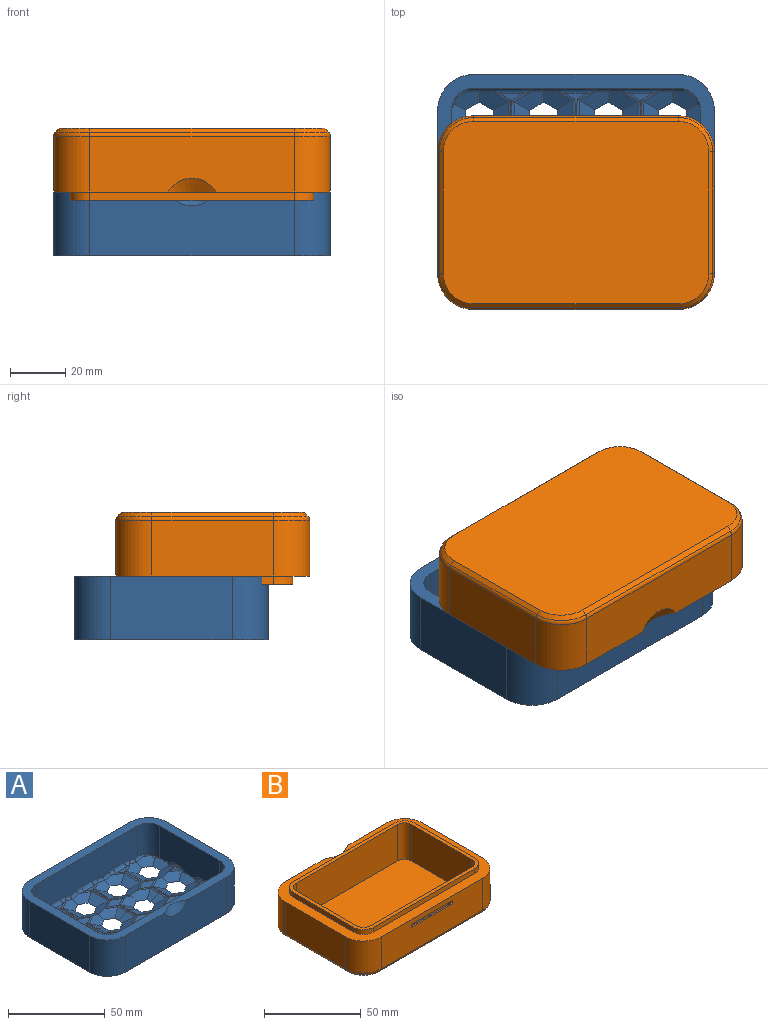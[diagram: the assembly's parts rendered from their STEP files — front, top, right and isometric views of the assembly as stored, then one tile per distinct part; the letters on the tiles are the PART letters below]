
ASSEMBLY  parts=2 mates=2
PART A: 247 faces, bbox 103.5x73.5x29 mm
  f0: plane 103.46x73.46mm, normal (0,0,1), area 1477.7mm2, adj f2,f4,f11,f16,f66,f67,f68,f74
  f1: plane 30x3mm, normal (0,-1,0), area 90mm2, adj f240,f241,f243,f244
  f2: plane 74x23mm, normal (0,1,0), area 1642mm2, adj f0,f3,f67,f127,f240,f241,f244,f245
  f3: plane 100x70mm, normal (0,0,-1), area 5815.7mm2, adj f2,f4,f7,f8,f9,f10,f21,f22
  f4: plane 44x23mm, normal (-1,0,0), area 1012mm2, adj f0,f3,f67,f185
  f5: plane 56x10.72mm, normal (0,0,1), area 99.6mm2, adj f12,f13,f39,f41,f43,f44,f47,f48
  f6: plane 25.94x10.76mm, normal (0,0,1), area 74.7mm2, adj f14,f17,f46,f77,f78,f106,f132,f135
  f7: plane 6.19x5.6mm, normal (-0.45,0,0.89), area 28.4mm2, adj f3,f14,f27,f129
  f8: plane 6.02x5.63mm, normal (0.45,0,0.89), area 27.7mm2, adj f3,f13,f28,f130
  f9: plane 12.21x5.58mm, normal (-0.45,0,0.89), area 56.1mm2, adj f3,f12,f32,f150
  f10: plane 12.1x7.11mm, normal (0.45,0,0.89), area 45.6mm2, adj f3,f11,f34,f65,f152,f183
  f11: plane 44x20.5mm, normal (1,0,0), area 852.2mm2, adj f0,f10,f35,f37,f59,f60,f62,f64
  f12: cylinder r=2mm len=13.25mm, axis (0,-1,0), area 11.8mm2, adj f5,f9,f39,f157
  f13: cylinder r=2mm len=6.55mm, axis (-0.01,1,0), area 5.8mm2, adj f5,f8,f43,f131
  f14: cylinder r=2mm len=6.72mm, axis (0.01,-1,0), area 6mm2, adj f6,f7,f46,f132
  f15: plane 14.57x7.49mm, normal (0,0,1), area 12.7mm2, adj f18,f19,f54,f79,f114
  f16: plane 74.05x19.52mm, normal (0,-1,0), area 1363.5mm2, adj f0,f19,f45,f49,f51,f53,f55,f56
  f17: cylinder r=2mm len=7.14mm, axis (-0.85,-0.53,0), area 6.4mm2, adj f6,f18,f26,f46,f78
  f18: cylinder r=2mm len=13.26mm, axis (0.03,-1,0), area 11.8mm2, adj f15,f17,f25,f54,f79
  f19: cylinder r=2mm len=7.49mm, axis (-1,0,0), area 23.5mm2, adj f15,f16,f56,f116
  f20: plane 1.98x1.71mm, normal (0,0,1), area 1.7mm2, adj f61,f62,f63
  f21: plane 10.68x6.52mm, normal (-0.21,-0.39,0.89), area 48.9mm2, adj f3,f22,f25,f54,f57,f58
  f22: plane 10.58x6.81mm, normal (0.24,-0.38,0.89), area 49.5mm2, adj f3,f21,f29,f52,f57
  f23: plane 10.58x6.67mm, normal (-0.22,-0.39,0.89), area 49.2mm2, adj f3,f24,f31,f48,f49
  f24: plane 8.46x6.65mm, normal (0.22,-0.39,0.89), area 46.3mm2, adj f3,f23,f35,f37,f40,f45,f49
  f25: plane 12.21x5.87mm, normal (-0.45,-0.01,0.89), area 56.1mm2, adj f3,f18,f21,f26
  f26: plane 10.58x7mm, normal (-0.24,0.38,0.89), area 50.2mm2, adj f3,f17,f25,f27,f30
  f27: plane 10.61x6.79mm, normal (-0.22,-0.39,0.89), area 49.1mm2, adj f3,f7,f26,f28,f30,f46
  f28: plane 10.58x6.87mm, normal (0.23,-0.39,0.89), area 49.9mm2, adj f3,f8,f27,f30,f43
  f29: plane 12.21x5.87mm, normal (0.45,0.01,0.89), area 56.1mm2, adj f3,f22,f30,f50
  f30: plane 10.69x6.67mm, normal (0.21,0.39,0.89), area 48.9mm2, adj f3,f26,f27,f28,f29,f47
  f31: plane 12.21x5.59mm, normal (-0.45,0,0.89), area 56.1mm2, adj f3,f23,f33,f44
  f32: plane 10.58x6.73mm, normal (-0.22,-0.39,0.89), area 49.6mm2, adj f3,f9,f33,f34,f39
  f33: plane 10.58x6.72mm, normal (-0.22,0.39,0.89), area 49.5mm2, adj f3,f31,f32,f34,f36,f41
  f34: plane 8.45x6.73mm, normal (0.22,-0.39,0.89), area 46.6mm2, adj f3,f10,f32,f33,f36,f63,f65
  f35: plane 12.09x7.11mm, normal (0.45,0,0.89), area 45.6mm2, adj f3,f11,f24,f36,f37,f59
  f36: plane 8.44x6.74mm, normal (0.22,0.39,0.89), area 46.6mm2, adj f3,f33,f34,f35,f59,f61
  f37: cylinder r=2mm len=5.56mm, axis (0,-0.92,-0.4), area 3.4mm2, adj f11,f24,f35,f38,f66
  f38: bspline ~2.22x1.86mm, area 0mm2, adj f37,f40,f66
  f39: cylinder r=2mm len=6.97mm, axis (0.87,-0.5,0), area 6mm2, adj f5,f12,f32,f41
  f40: cylinder r=2mm len=4.19mm, axis (0.87,0.5,0), area 1.8mm2, adj f24,f38,f42,f66
  f41: cylinder r=2mm len=6.96mm, axis (-0.87,-0.5,0), area 6mm2, adj f5,f33,f39,f44
  f42: bspline ~4.88x2.29mm, area 1.4mm2, adj f40,f45,f66
  f43: cylinder r=2mm len=7.04mm, axis (0.86,0.51,0), area 6.1mm2, adj f5,f13,f28,f47
  f44: cylinder r=2mm len=13.25mm, axis (0,-1,0), area 11.8mm2, adj f5,f31,f41,f48
  f45: cylinder r=2mm len=5.08mm, axis (-0.97,0,0.24), area 9.2mm2, adj f16,f24,f42,f49,f66
  f46: cylinder r=2mm len=6.89mm, axis (0.87,-0.49,0), area 5.9mm2, adj f6,f14,f17,f27
  f47: cylinder r=2mm len=6.76mm, axis (-0.88,0.47,0), area 5.7mm2, adj f5,f30,f43,f50
  f48: cylinder r=2mm len=6.86mm, axis (0.87,-0.5,0), area 5.2mm2, adj f5,f23,f44,f51
  f49: cylinder r=2mm len=5.05mm, axis (-0.97,0,-0.24), area 10.7mm2, adj f16,f23,f24,f45,f51
  f50: cylinder r=2mm len=13.27mm, axis (-0.03,1,0), area 11.8mm2, adj f5,f29,f47,f52
  f51: bspline ~5.67x2.36mm, area 9.1mm2, adj f16,f48,f49,f53
  f52: cylinder r=2mm len=6.98mm, axis (0.85,0.53,0), area 5.5mm2, adj f5,f22,f50,f55
  f53: cylinder r=2mm len=7.98mm, axis (-1,0,0), area 25.1mm2, adj f5,f16,f51,f55
  f54: cylinder r=2mm len=6.7mm, axis (0.88,-0.47,0), area 4.8mm2, adj f15,f18,f21,f56
  f55: bspline ~3.39x2.21mm, area 8.6mm2, adj f16,f52,f53,f57
  f56: bspline ~3.79x2.21mm, area 9.7mm2, adj f16,f19,f54,f58
  f57: cylinder r=2mm len=4.86mm, axis (-0.97,0,0.26), area 10.3mm2, adj f16,f21,f22,f55,f58
  f58: cylinder r=2mm len=5.28mm, axis (-0.97,0,-0.23), area 11.1mm2, adj f16,f21,f56,f57
  f59: cylinder r=2mm len=5.58mm, axis (0,-0.92,0.4), area 10.7mm2, adj f11,f35,f36,f60
  f60: bspline ~2.21x2.07mm, area 4.7mm2, adj f11,f59,f61,f62
  f61: cylinder r=2mm len=4.39mm, axis (-0.87,0.5,0), area 3mm2, adj f20,f36,f60,f63
  f62: cylinder r=2mm len=2mm, axis (0,-1,0), area 6.2mm2, adj f11,f20,f60,f64
  f63: cylinder r=2mm len=4.39mm, axis (0.87,0.5,0), area 3mm2, adj f20,f34,f61,f64
  f64: bspline ~2.69x2.31mm, area 4.7mm2, adj f11,f62,f63,f65
  f65: cylinder r=2mm len=5.57mm, axis (0,-0.92,-0.4), area 10.6mm2, adj f10,f11,f34,f64
  f66: cylinder r=8mm len=20.18mm, axis (0,0,-1), area 249.6mm2, adj f0,f11,f16,f37,f38,f40,f42,f45
  f67: cylinder r=13mm len=23mm, axis (0,0,1), area 469.7mm2, adj f0,f2,f3,f4
  f68: plane 44x23mm, normal (1,0,0), area 1012mm2, adj f0,f3,f127,f239
  f69: plane 56x10.72mm, normal (0,0,1), area 99.6mm2, adj f75,f76,f99,f101,f103,f104,f107,f108
  f70: plane 6.19x5.6mm, normal (0.45,0,0.89), area 28.4mm2, adj f3,f77,f87,f186
  f71: plane 6.02x5.63mm, normal (-0.45,0,0.89), area 27.7mm2, adj f3,f76,f88,f187
  f72: plane 12.21x5.58mm, normal (0.45,0,0.89), area 56.1mm2, adj f3,f75,f92,f204
  f73: plane 12.1x7.11mm, normal (-0.45,0,0.89), area 45.6mm2, adj f3,f74,f94,f125,f206,f237
  f74: plane 44x20.5mm, normal (-1,0,0), area 852.2mm2, adj f0,f73,f95,f97,f119,f120,f122,f124
  f75: cylinder r=2mm len=13.25mm, axis (0,-1,0), area 11.8mm2, adj f69,f72,f99,f211
  f76: cylinder r=2mm len=6.55mm, axis (0.01,1,0), area 5.8mm2, adj f69,f71,f103,f188
  f77: cylinder r=2mm len=6.72mm, axis (-0.01,-1,0), area 6mm2, adj f6,f70,f106,f189
  f78: cylinder r=2mm len=7.14mm, axis (0.85,-0.53,0), area 6.4mm2, adj f6,f17,f79,f86,f106
  f79: cylinder r=2mm len=13.26mm, axis (-0.03,-1,0), area 11.8mm2, adj f15,f18,f78,f85,f114
  f80: plane 1.98x1.71mm, normal (0,0,1), area 1.7mm2, adj f121,f122,f123
  f81: plane 10.68x6.52mm, normal (0.21,-0.39,0.89), area 48.9mm2, adj f3,f82,f85,f114,f117,f118
  f82: plane 10.58x6.81mm, normal (-0.24,-0.38,0.89), area 49.5mm2, adj f3,f81,f89,f112,f117
  f83: plane 10.58x6.67mm, normal (0.22,-0.39,0.89), area 49.2mm2, adj f3,f84,f91,f108,f109
  f84: plane 8.46x6.65mm, normal (-0.22,-0.39,0.89), area 46.3mm2, adj f3,f83,f95,f97,f100,f105,f109
  f85: plane 12.21x5.87mm, normal (0.45,-0.01,0.89), area 56.1mm2, adj f3,f79,f81,f86
  f86: plane 10.58x7mm, normal (0.24,0.38,0.89), area 50.2mm2, adj f3,f78,f85,f87,f90
  f87: plane 10.61x6.79mm, normal (0.22,-0.39,0.89), area 49.1mm2, adj f3,f70,f86,f88,f90,f106
  f88: plane 10.58x6.87mm, normal (-0.23,-0.39,0.89), area 49.9mm2, adj f3,f71,f87,f90,f103
  f89: plane 12.21x5.87mm, normal (-0.45,0.01,0.89), area 56.1mm2, adj f3,f82,f90,f110
  f90: plane 10.69x6.67mm, normal (-0.21,0.39,0.89), area 48.9mm2, adj f3,f86,f87,f88,f89,f107
  f91: plane 12.21x5.59mm, normal (0.45,0,0.89), area 56.1mm2, adj f3,f83,f93,f104
  f92: plane 10.58x6.73mm, normal (0.22,-0.39,0.89), area 49.6mm2, adj f3,f72,f93,f94,f99
  f93: plane 10.58x6.72mm, normal (0.22,0.39,0.89), area 49.5mm2, adj f3,f91,f92,f94,f96,f101
  f94: plane 8.45x6.73mm, normal (-0.22,-0.39,0.89), area 46.6mm2, adj f3,f73,f92,f93,f96,f123,f125
  f95: plane 12.09x7.11mm, normal (-0.45,0,0.89), area 45.6mm2, adj f3,f74,f84,f96,f97,f119
  f96: plane 8.44x6.74mm, normal (-0.22,0.39,0.89), area 46.6mm2, adj f3,f93,f94,f95,f119,f121
  f97: cylinder r=2mm len=5.56mm, axis (0,-0.92,-0.4), area 3.4mm2, adj f74,f84,f95,f98,f126
  f98: bspline ~2.22x1.86mm, area 0mm2, adj f97,f100,f126
  f99: cylinder r=2mm len=6.97mm, axis (-0.87,-0.5,0), area 6mm2, adj f69,f75,f92,f101
  f100: cylinder r=2mm len=4.19mm, axis (-0.87,0.5,0), area 1.8mm2, adj f84,f98,f102,f126
  f101: cylinder r=2mm len=6.96mm, axis (0.87,-0.5,0), area 6mm2, adj f69,f93,f99,f104
  f102: bspline ~4.56x2.29mm, area 1.4mm2, adj f100,f105,f126
  f103: cylinder r=2mm len=7.04mm, axis (-0.86,0.51,0), area 6.1mm2, adj f69,f76,f88,f107
  f104: cylinder r=2mm len=13.25mm, axis (0,-1,0), area 11.8mm2, adj f69,f91,f101,f108
  f105: cylinder r=2mm len=5.08mm, axis (0.97,0,0.24), area 9.2mm2, adj f16,f84,f102,f109,f126
  f106: cylinder r=2mm len=6.89mm, axis (-0.87,-0.49,0), area 5.9mm2, adj f6,f77,f78,f87
  f107: cylinder r=2mm len=6.76mm, axis (0.88,0.47,0), area 5.7mm2, adj f69,f90,f103,f110
  f108: cylinder r=2mm len=6.86mm, axis (-0.87,-0.5,0), area 5.2mm2, adj f69,f83,f104,f111
  f109: cylinder r=2mm len=5.05mm, axis (0.97,0,-0.24), area 10.7mm2, adj f16,f83,f84,f105,f111
  f110: cylinder r=2mm len=13.27mm, axis (0.03,1,0), area 11.8mm2, adj f69,f89,f107,f112
  f111: bspline ~5.67x2.36mm, area 9.1mm2, adj f16,f108,f109,f113
  f112: cylinder r=2mm len=6.98mm, axis (-0.85,0.53,0), area 5.5mm2, adj f69,f82,f110,f115
  f113: cylinder r=2mm len=7.98mm, axis (1,0,0), area 25.1mm2, adj f16,f69,f111,f115
  f114: cylinder r=2mm len=6.7mm, axis (-0.88,-0.47,0), area 4.8mm2, adj f15,f79,f81,f116
  f115: bspline ~3.39x2.21mm, area 8.6mm2, adj f16,f112,f113,f117
  f116: bspline ~3.79x2.21mm, area 9.7mm2, adj f16,f19,f114,f118
  f117: cylinder r=2mm len=4.86mm, axis (0.97,0,0.26), area 10.3mm2, adj f16,f81,f82,f115,f118
  f118: cylinder r=2mm len=5.28mm, axis (0.97,0,-0.23), area 11.1mm2, adj f16,f81,f116,f117
  f119: cylinder r=2mm len=5.58mm, axis (0,-0.92,0.4), area 10.7mm2, adj f74,f95,f96,f120
  f120: bspline ~2.21x2.07mm, area 4.7mm2, adj f74,f119,f121,f122
  f121: cylinder r=2mm len=4.39mm, axis (0.87,0.5,0), area 3mm2, adj f80,f96,f120,f123
  f122: cylinder r=2mm len=2mm, axis (0,-1,0), area 6.2mm2, adj f74,f80,f120,f124
  f123: cylinder r=2mm len=4.39mm, axis (-0.87,0.5,0), area 3mm2, adj f80,f94,f121,f124
  f124: bspline ~2.69x2.31mm, area 4.7mm2, adj f74,f122,f123,f125
  f125: cylinder r=2mm len=5.57mm, axis (0,-0.92,-0.4), area 10.6mm2, adj f73,f74,f94,f124
  f126: cylinder r=8mm len=20.18mm, axis (0,0,-1), area 249.6mm2, adj f0,f16,f74,f97,f98,f100,f102,f105
  f127: cylinder r=13mm len=23mm, axis (0,0,1), area 469.7mm2, adj f0,f2,f3,f68
  f128: plane 74x23mm, normal (0,-1,0), area 1640.6mm2, adj f0,f3,f185,f239,f246
  f129: plane 6.19x5.6mm, normal (-0.45,0,0.89), area 28.4mm2, adj f3,f7,f132,f145
  f130: plane 6.02x5.63mm, normal (0.45,0,0.89), area 27.7mm2, adj f3,f8,f131,f146
  f131: cylinder r=2mm len=6.55mm, axis (-0.01,-1,0), area 5.8mm2, adj f5,f13,f130,f161
  f132: cylinder r=2mm len=6.72mm, axis (0.01,1,0), area 6mm2, adj f6,f14,f129,f164
  f133: plane 14.57x7.49mm, normal (0,0,1), area 12.7mm2, adj f136,f137,f172,f191,f226
  f134: plane 74.05x19.52mm, normal (0,1,0), area 1363.5mm2, adj f0,f137,f163,f167,f169,f171,f173,f174
  f135: cylinder r=2mm len=7.14mm, axis (-0.85,0.53,0), area 6.4mm2, adj f6,f136,f144,f164,f190
  f136: cylinder r=2mm len=13.26mm, axis (0.03,1,0), area 11.8mm2, adj f133,f135,f143,f172,f191
  f137: cylinder r=2mm len=7.49mm, axis (-1,0,0), area 23.5mm2, adj f133,f134,f174,f228
  f138: plane 1.98x1.71mm, normal (0,0,1), area 1.7mm2, adj f179,f180,f181
  f139: plane 10.68x6.52mm, normal (-0.21,0.39,0.89), area 48.9mm2, adj f3,f140,f143,f172,f175,f176
  f140: plane 10.58x6.81mm, normal (0.24,0.38,0.89), area 49.5mm2, adj f3,f139,f147,f170,f175
  f141: plane 10.58x6.67mm, normal (-0.22,0.39,0.89), area 49.2mm2, adj f3,f142,f149,f166,f167
  f142: plane 8.46x6.65mm, normal (0.22,0.39,0.89), area 46.3mm2, adj f3,f141,f153,f155,f158,f163,f167
  f143: plane 12.21x5.87mm, normal (-0.45,0.01,0.89), area 56.1mm2, adj f3,f136,f139,f144
  f144: plane 10.58x7mm, normal (-0.24,-0.38,0.89), area 50.2mm2, adj f3,f135,f143,f145,f148
  f145: plane 10.61x6.79mm, normal (-0.22,0.39,0.89), area 49.1mm2, adj f3,f129,f144,f146,f148,f164
  f146: plane 10.58x6.87mm, normal (0.23,0.39,0.89), area 49.9mm2, adj f3,f130,f145,f148,f161
  f147: plane 12.21x5.87mm, normal (0.45,-0.01,0.89), area 56.1mm2, adj f3,f140,f148,f168
  f148: plane 10.69x6.67mm, normal (0.21,-0.39,0.89), area 48.9mm2, adj f3,f144,f145,f146,f147,f165
  f149: plane 12.21x5.59mm, normal (-0.45,0,0.89), area 56.1mm2, adj f3,f141,f151,f162
  f150: plane 10.58x6.73mm, normal (-0.22,0.39,0.89), area 49.6mm2, adj f3,f9,f151,f152,f157
  f151: plane 10.58x6.72mm, normal (-0.22,-0.39,0.89), area 49.5mm2, adj f3,f149,f150,f152,f154,f159
  f152: plane 8.45x6.73mm, normal (0.22,0.39,0.89), area 46.6mm2, adj f3,f10,f150,f151,f154,f181,f183
  f153: plane 12.09x7.11mm, normal (0.45,0,0.89), area 45.6mm2, adj f3,f11,f142,f154,f155,f177
  f154: plane 8.44x6.74mm, normal (0.22,-0.39,0.89), area 46.6mm2, adj f3,f151,f152,f153,f177,f179
  f155: cylinder r=2mm len=5.56mm, axis (0,0.92,-0.4), area 3.4mm2, adj f11,f142,f153,f156,f184
  f156: bspline ~2.22x1.86mm, area 0mm2, adj f155,f158,f184
  f157: cylinder r=2mm len=6.97mm, axis (0.87,0.5,0), area 6mm2, adj f5,f12,f150,f159
  f158: cylinder r=2mm len=4.19mm, axis (0.87,-0.5,0), area 1.8mm2, adj f142,f156,f160,f184
  f159: cylinder r=2mm len=6.96mm, axis (-0.87,0.5,0), area 6mm2, adj f5,f151,f157,f162
  f160: bspline ~4.56x2.29mm, area 1.4mm2, adj f158,f163,f184
  f161: cylinder r=2mm len=7.04mm, axis (0.86,-0.51,0), area 6.1mm2, adj f5,f131,f146,f165
  f162: cylinder r=2mm len=13.25mm, axis (0,1,0), area 11.8mm2, adj f5,f149,f159,f166
  f163: cylinder r=2mm len=5.08mm, axis (-0.97,0,0.24), area 9.2mm2, adj f134,f142,f160,f167,f184
  f164: cylinder r=2mm len=6.89mm, axis (0.87,0.49,0), area 5.9mm2, adj f6,f132,f135,f145
  f165: cylinder r=2mm len=6.76mm, axis (-0.88,-0.47,0), area 5.7mm2, adj f5,f148,f161,f168
  f166: cylinder r=2mm len=6.86mm, axis (0.87,0.5,0), area 5.2mm2, adj f5,f141,f162,f169
  f167: cylinder r=2mm len=5.05mm, axis (-0.97,0,-0.24), area 10.7mm2, adj f134,f141,f142,f163,f169
  f168: cylinder r=2mm len=13.27mm, axis (-0.03,-1,0), area 11.8mm2, adj f5,f147,f165,f170
  f169: bspline ~5.67x2.36mm, area 9.1mm2, adj f134,f166,f167,f171
  f170: cylinder r=2mm len=6.98mm, axis (0.85,-0.53,0), area 5.5mm2, adj f5,f140,f168,f173
  f171: cylinder r=2mm len=7.98mm, axis (-1,0,0), area 25.1mm2, adj f5,f134,f169,f173
  f172: cylinder r=2mm len=6.7mm, axis (0.88,0.47,0), area 4.8mm2, adj f133,f136,f139,f174
  f173: bspline ~3.39x2.21mm, area 8.6mm2, adj f134,f170,f171,f175
  f174: bspline ~3.79x2.21mm, area 9.7mm2, adj f134,f137,f172,f176
  f175: cylinder r=2mm len=4.86mm, axis (-0.97,0,0.26), area 10.3mm2, adj f134,f139,f140,f173,f176
  f176: cylinder r=2mm len=5.28mm, axis (-0.97,0,-0.23), area 11.1mm2, adj f134,f139,f174,f175
  f177: cylinder r=2mm len=5.58mm, axis (0,0.92,0.4), area 10.7mm2, adj f11,f153,f154,f178
  f178: bspline ~2.21x2.07mm, area 4.7mm2, adj f11,f177,f179,f180
  f179: cylinder r=2mm len=4.39mm, axis (-0.87,-0.5,0), area 3mm2, adj f138,f154,f178,f181
  f180: cylinder r=2mm len=2mm, axis (0,1,0), area 6.2mm2, adj f11,f138,f178,f182
  f181: cylinder r=2mm len=4.39mm, axis (0.87,-0.5,0), area 3mm2, adj f138,f152,f179,f182
  f182: bspline ~2.69x2.31mm, area 4.7mm2, adj f11,f180,f181,f183
  f183: cylinder r=2mm len=5.57mm, axis (0,0.92,-0.4), area 10.6mm2, adj f10,f11,f152,f182
  f184: cylinder r=8mm len=20.18mm, axis (0,0,-1), area 249.6mm2, adj f0,f11,f134,f155,f156,f158,f160,f163
  f185: cylinder r=13mm len=23mm, axis (0,0,1), area 469.7mm2, adj f0,f3,f4,f128
  f186: plane 6.19x5.6mm, normal (0.45,0,0.89), area 28.4mm2, adj f3,f70,f189,f199
  f187: plane 6.02x5.63mm, normal (-0.45,0,0.89), area 27.7mm2, adj f3,f71,f188,f200
  f188: cylinder r=2mm len=6.55mm, axis (0.01,-1,0), area 5.8mm2, adj f69,f76,f187,f215
  f189: cylinder r=2mm len=6.72mm, axis (-0.01,1,0), area 6mm2, adj f6,f77,f186,f218
  f190: cylinder r=2mm len=7.14mm, axis (0.85,0.53,0), area 6.4mm2, adj f6,f135,f191,f198,f218
  f191: cylinder r=2mm len=13.26mm, axis (-0.03,1,0), area 11.8mm2, adj f133,f136,f190,f197,f226
  f192: plane 1.98x1.71mm, normal (0,0,1), area 1.7mm2, adj f233,f234,f235
  f193: plane 10.68x6.52mm, normal (0.21,0.39,0.89), area 48.9mm2, adj f3,f194,f197,f226,f229,f230
  f194: plane 10.58x6.81mm, normal (-0.24,0.38,0.89), area 49.5mm2, adj f3,f193,f201,f224,f229
  f195: plane 10.58x6.67mm, normal (0.22,0.39,0.89), area 49.2mm2, adj f3,f196,f203,f220,f221
  f196: plane 8.46x6.65mm, normal (-0.22,0.39,0.89), area 46.3mm2, adj f3,f195,f207,f209,f212,f217,f221
  f197: plane 12.21x5.87mm, normal (0.45,0.01,0.89), area 56.1mm2, adj f3,f191,f193,f198
  f198: plane 10.58x7mm, normal (0.24,-0.38,0.89), area 50.2mm2, adj f3,f190,f197,f199,f202
  f199: plane 10.61x6.79mm, normal (0.22,0.39,0.89), area 49.1mm2, adj f3,f186,f198,f200,f202,f218
  f200: plane 10.58x6.87mm, normal (-0.23,0.39,0.89), area 49.9mm2, adj f3,f187,f199,f202,f215
  f201: plane 12.21x5.87mm, normal (-0.45,-0.01,0.89), area 56.1mm2, adj f3,f194,f202,f222
  f202: plane 10.69x6.67mm, normal (-0.21,-0.39,0.89), area 48.9mm2, adj f3,f198,f199,f200,f201,f219
  f203: plane 12.21x5.59mm, normal (0.45,0,0.89), area 56.1mm2, adj f3,f195,f205,f216
  f204: plane 10.58x6.73mm, normal (0.22,0.39,0.89), area 49.6mm2, adj f3,f72,f205,f206,f211
  f205: plane 10.58x6.72mm, normal (0.22,-0.39,0.89), area 49.5mm2, adj f3,f203,f204,f206,f208,f213
  f206: plane 8.45x6.73mm, normal (-0.22,0.39,0.89), area 46.6mm2, adj f3,f73,f204,f205,f208,f235,f237
  f207: plane 12.09x7.11mm, normal (-0.45,0,0.89), area 45.6mm2, adj f3,f74,f196,f208,f209,f231
  f208: plane 8.44x6.74mm, normal (-0.22,-0.39,0.89), area 46.6mm2, adj f3,f205,f206,f207,f231,f233
  f209: cylinder r=2mm len=5.56mm, axis (0,0.92,-0.4), area 3.4mm2, adj f74,f196,f207,f210,f238
  f210: bspline ~2.22x1.86mm, area 0mm2, adj f209,f212,f238
  f211: cylinder r=2mm len=6.97mm, axis (-0.87,0.5,0), area 6mm2, adj f69,f75,f204,f213
  f212: cylinder r=2mm len=4.19mm, axis (-0.87,-0.5,0), area 1.8mm2, adj f196,f210,f214,f238
  f213: cylinder r=2mm len=6.96mm, axis (0.87,0.5,0), area 6mm2, adj f69,f205,f211,f216
  f214: bspline ~4.88x2.29mm, area 1.4mm2, adj f212,f217,f238
  f215: cylinder r=2mm len=7.04mm, axis (-0.86,-0.51,0), area 6.1mm2, adj f69,f188,f200,f219
  f216: cylinder r=2mm len=13.25mm, axis (0,1,0), area 11.8mm2, adj f69,f203,f213,f220
  f217: cylinder r=2mm len=5.08mm, axis (0.97,0,0.24), area 9.2mm2, adj f134,f196,f214,f221,f238
  f218: cylinder r=2mm len=6.89mm, axis (-0.87,0.49,0), area 5.9mm2, adj f6,f189,f190,f199
  f219: cylinder r=2mm len=6.76mm, axis (0.88,-0.47,0), area 5.7mm2, adj f69,f202,f215,f222
  f220: cylinder r=2mm len=6.86mm, axis (-0.87,0.5,0), area 5.2mm2, adj f69,f195,f216,f223
  f221: cylinder r=2mm len=5.05mm, axis (0.97,0,-0.24), area 10.7mm2, adj f134,f195,f196,f217,f223
  f222: cylinder r=2mm len=13.27mm, axis (0.03,-1,0), area 11.8mm2, adj f69,f201,f219,f224
  f223: bspline ~5.67x2.36mm, area 9.1mm2, adj f134,f220,f221,f225
  f224: cylinder r=2mm len=6.98mm, axis (-0.85,-0.53,0), area 5.5mm2, adj f69,f194,f222,f227
  f225: cylinder r=2mm len=7.98mm, axis (1,0,0), area 25.1mm2, adj f69,f134,f223,f227
  f226: cylinder r=2mm len=6.7mm, axis (-0.88,0.47,0), area 4.8mm2, adj f133,f191,f193,f228
  f227: bspline ~3.39x2.21mm, area 8.6mm2, adj f134,f224,f225,f229
  f228: bspline ~3.79x2.21mm, area 9.7mm2, adj f134,f137,f226,f230
  f229: cylinder r=2mm len=4.86mm, axis (0.97,0,0.26), area 10.3mm2, adj f134,f193,f194,f227,f230
  f230: cylinder r=2mm len=5.28mm, axis (0.97,0,-0.23), area 11.1mm2, adj f134,f193,f228,f229
  f231: cylinder r=2mm len=5.58mm, axis (0,0.92,0.4), area 10.7mm2, adj f74,f207,f208,f232
  f232: bspline ~2.21x2.07mm, area 4.7mm2, adj f74,f231,f233,f234
  f233: cylinder r=2mm len=4.39mm, axis (0.87,-0.5,0), area 3mm2, adj f192,f208,f232,f235
  f234: cylinder r=2mm len=2mm, axis (0,1,0), area 6.2mm2, adj f74,f192,f232,f236
  f235: cylinder r=2mm len=4.39mm, axis (-0.87,-0.5,0), area 3mm2, adj f192,f206,f233,f236
  f236: bspline ~2.69x2.31mm, area 4.7mm2, adj f74,f234,f235,f237
  f237: cylinder r=2mm len=5.57mm, axis (0,0.92,-0.4), area 10.6mm2, adj f73,f74,f206,f236
  f238: cylinder r=8mm len=20.18mm, axis (0,0,-1), area 249.6mm2, adj f0,f74,f134,f209,f210,f212,f214,f217
  f239: cylinder r=13mm len=23mm, axis (0,0,1), area 469.7mm2, adj f0,f3,f68,f128
  f240: plane 5x4mm, normal (-1,0,0), area 17mm2, adj f1,f2,f242,f243,f244,f245
  f241: plane 5x4mm, normal (1,0,0), area 17mm2, adj f1,f2,f242,f243,f244,f245
  f242: plane 30x5mm, normal (0,1,0), area 150mm2, adj f240,f241,f243,f245
  f243: plane 30x3mm, normal (0,0,1), area 90mm2, adj f1,f240,f241,f242
  f244: plane 30x1mm, normal (0,0,1), area 30mm2, adj f1,f2,f240,f241
  f245: plane 30x4mm, normal (0,0,-1), area 120mm2, adj f2,f240,f241,f242
  f246: cone r=5mm half-angle=59deg, axis (0,-1,0), area 50.9mm2, adj f0,f128
PART B: 52 faces, bbox 102.1x72.1x26 mm
  f0: plane 74x20.17mm, normal (0,1,0), area 1431.3mm2, adj f1,f8,f9,f50,f51
  f1: plane 100x70mm, normal (0,0,1), area 1760.8mm2, adj f0,f2,f3,f4,f6,f7,f8,f9
  f2: plane 44x20.17mm, normal (-1,0,0), area 887.5mm2, adj f1,f3,f8,f47
  f3: cylinder r=13mm len=20.17mm, axis (0,0,-1), area 411.9mm2, adj f1,f2,f4,f45
  f4: plane 74x20.17mm, normal (0,-1,0), area 1432.7mm2, adj f1,f3,f7,f10,f12,f15,f16,f43
  f5: plane 96x66mm, normal (0,0,-1), area 6232.1mm2, adj f35,f36,f37,f38,f39,f40,f41,f42
  f6: plane 44x20.17mm, normal (1,0,0), area 887.5mm2, adj f1,f7,f9,f46
  f7: cylinder r=13mm len=20.17mm, axis (0,0,-1), area 411.9mm2, adj f1,f4,f6,f44
  f8: cylinder r=13mm len=20.17mm, axis (0,0,-1), area 411.9mm2, adj f0,f1,f2,f49
  f9: cylinder r=13mm len=20.17mm, axis (0,0,-1), area 411.9mm2, adj f0,f1,f6,f48
  f10: plane 5x4mm, normal (1,0,0), area 17mm2, adj f4,f11,f13,f14,f15,f16
  f11: plane 30x3mm, normal (0,1,0), area 90mm2, adj f10,f12,f14,f15
  f12: plane 5x4mm, normal (-1,0,0), area 17mm2, adj f4,f11,f13,f14,f15,f16
  f13: plane 30x5mm, normal (0,-1,0), area 150mm2, adj f10,f12,f14,f16
  f14: plane 30x3mm, normal (0,0,1), area 90mm2, adj f10,f11,f12,f13
  f15: plane 30x1mm, normal (0,0,1), area 30mm2, adj f4,f10,f11,f12
  f16: plane 30x4mm, normal (0,0,-1), area 120mm2, adj f4,f10,f12,f13
  f17: plane 44x23mm, normal (1,0,0), area 1012mm2, adj f19,f20,f29,f34
  f18: plane 74x23mm, normal (0,-1,0), area 1702mm2, adj f19,f20,f25,f34
  f19: cylinder r=5mm len=23mm, axis (0,0,-1), area 180.6mm2, adj f17,f18,f20,f34
  f20: plane 88x58mm, normal (0,0,1), area 547.4mm2, adj f17,f18,f19,f21,f22,f23,f24,f25
  f21: plane 74x3mm, normal (0,1,0), area 222mm2, adj f1,f20,f22,f26
  f22: cylinder r=7mm len=7mm, axis (0,0,-1), area 33mm2, adj f1,f20,f21,f23
  f23: plane 44x3mm, normal (-1,0,0), area 132mm2, adj f1,f20,f22,f31
  f24: plane 44x23mm, normal (-1,0,0), area 1012mm2, adj f20,f25,f32,f34
  f25: cylinder r=5mm len=23mm, axis (0,0,-1), area 180.6mm2, adj f18,f20,f24,f34
  f26: cylinder r=7mm len=7mm, axis (0,0,-1), area 33mm2, adj f1,f20,f21,f27
  f27: plane 44x3mm, normal (1,0,0), area 132mm2, adj f1,f20,f26,f33
  f28: plane 74x23mm, normal (0,1,0), area 1702mm2, adj f20,f29,f32,f34
  f29: cylinder r=5mm len=23mm, axis (0,0,-1), area 180.6mm2, adj f17,f20,f28,f34
  f30: plane 74x3mm, normal (0,-1,0), area 222mm2, adj f1,f20,f31,f33
  f31: cylinder r=7mm len=7mm, axis (0,0,-1), area 33mm2, adj f1,f20,f23,f30
  f32: cylinder r=5mm len=23mm, axis (0,0,-1), area 180.6mm2, adj f20,f24,f28,f34
  f33: cylinder r=7mm len=7mm, axis (0,0,-1), area 33mm2, adj f1,f20,f27,f30
  f34: plane 84x54mm, normal (0,0,1), area 4514.5mm2, adj f17,f18,f19,f24,f25,f28,f29,f32
  f35: plane 74x1.41mm, normal (0,-0.71,-0.71), area 148mm2, adj f5,f36,f37,f43
  f36: cone r=13mm half-angle=45deg, axis (0,0,1), area 36.8mm2, adj f5,f35,f38,f45
  f37: cone r=11mm half-angle=45deg, axis (0,0,1), area 36.8mm2, adj f5,f35,f39,f44
  f38: plane 44x1.41mm, normal (-0.71,0,-0.71), area 88mm2, adj f5,f36,f40,f47
  f39: plane 44x1.41mm, normal (0.71,0,-0.71), area 88mm2, adj f5,f37,f41,f46
  f40: cone r=11mm half-angle=45deg, axis (0,0,1), area 36.8mm2, adj f5,f38,f42,f49
  f41: cone r=13mm half-angle=45deg, axis (0,0,1), area 36.8mm2, adj f5,f39,f42,f48
  f42: plane 74x1.41mm, normal (0,0.71,-0.71), area 148mm2, adj f5,f40,f41,f50
  f43: cylinder r=2mm len=74mm, axis (1,0,0), area 116.2mm2, adj f4,f35,f44,f45
  f44: torus R=11mm, axis (0,0,-1), area 31.6mm2, adj f7,f37,f43,f46
  f45: torus R=11mm, axis (0,0,-1), area 31.6mm2, adj f3,f36,f43,f47
  f46: cylinder r=2mm len=44mm, axis (0,1,0), area 69.1mm2, adj f6,f39,f44,f48
  f47: cylinder r=2mm len=44mm, axis (0,-1,0), area 69.1mm2, adj f2,f38,f45,f49
  f48: torus R=11mm, axis (0,0,-1), area 31.6mm2, adj f9,f41,f46,f50
  f49: torus R=11mm, axis (0,0,-1), area 31.6mm2, adj f8,f40,f47,f50
  f50: cylinder r=2mm len=74mm, axis (-1,0,0), area 116.2mm2, adj f0,f42,f48,f49
  f51: cone r=5mm half-angle=59deg, axis (0,1,0), area 71.6mm2, adj f0,f1
PLACE A t=(-2.47,-45.02,26.77)mm
PLACE B rot(axis=(1,0,0),180deg) t=(-2.47,39.98,72.77)mm
MATE parallel B.f4 <-> A.f2  axis (0,1,0) through (-2.47,-25.02,60.11)mm
MATE parallel B.f2 <-> A.f4  axis (-1,0,0) through (-52.47,-60.02,59.86)mm
